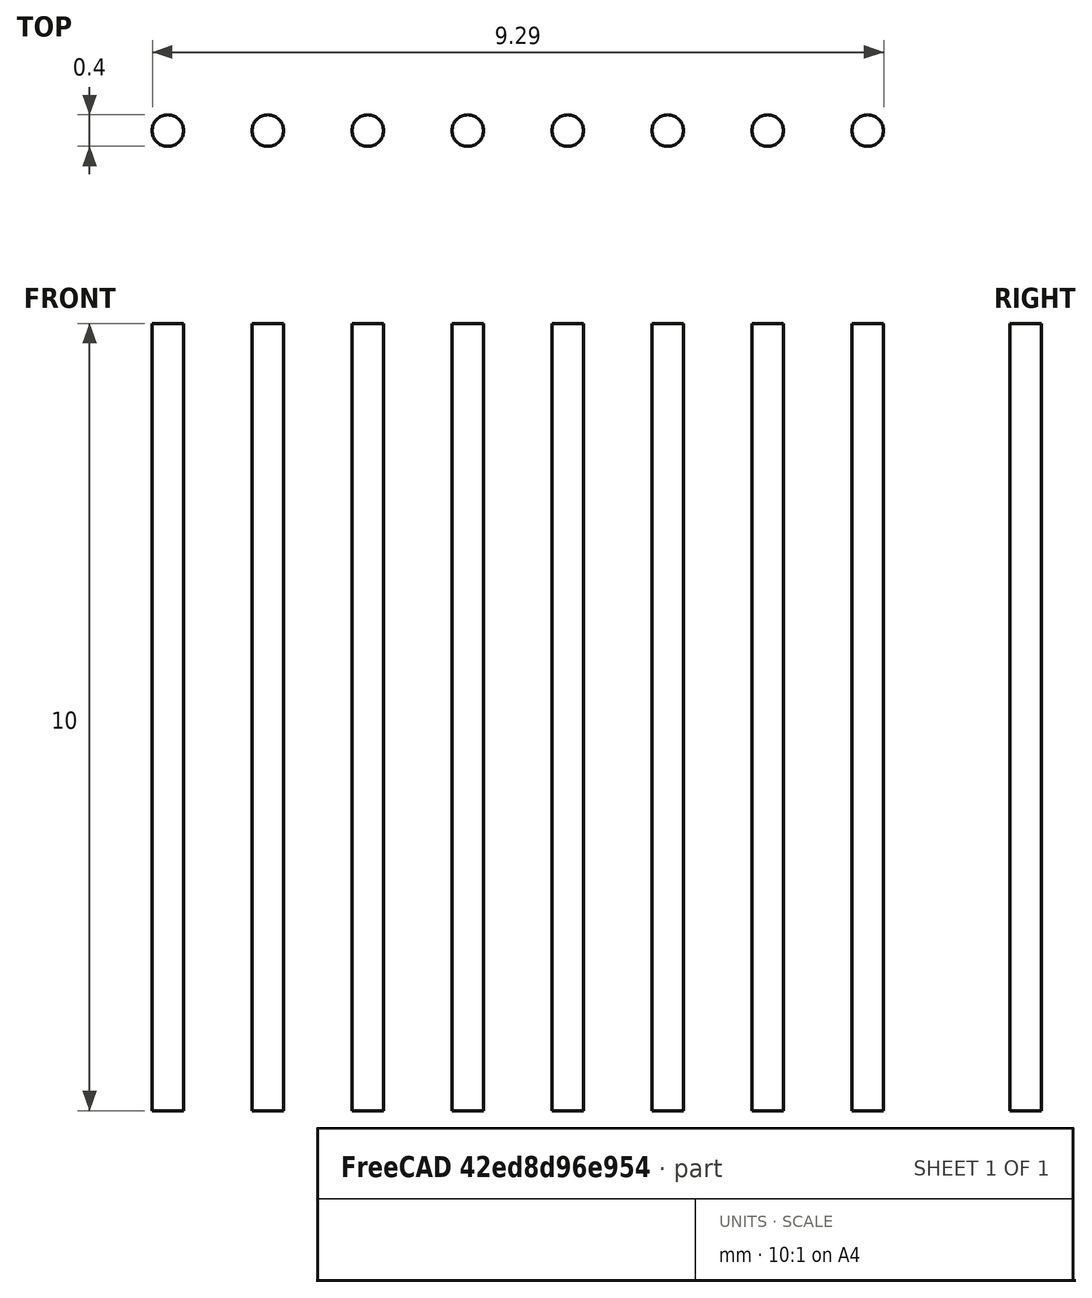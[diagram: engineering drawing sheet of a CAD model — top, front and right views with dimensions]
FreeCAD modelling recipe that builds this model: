
FCSTD DOCUMENT  (FreeCAD 0.14R3702 (Git))
Label: LCD
License: CC-BY 3.0
LicenseURL: http://creativecommons.org/licenses/by/3.0/
objects: Sketcher::SketchObject×2, Part::Cylinder×1, Part::FeaturePython×1, Part::Part2DObjectPython×1
note: 5 computed .brp shape members not serialized (recipe doc carries the construction recipe); baked Part::Feature solids carry a one-line shape summary decoded from their .brp

FEATURE [Sketcher::SketchObject] Sketch
  sketch-geometry (16):
    g0: LineSegment StartX=0 StartY=20.7 StartZ=0 EndX=51.2 EndY=20.7 EndZ=0
    g1: LineSegment StartX=51.2 StartY=20.7 StartZ=0 EndX=51.2 EndY=0 EndZ=0
    g2: LineSegment StartX=51.2 StartY=0 StartZ=0 EndX=0 EndY=0 EndZ=0
    g3: LineSegment StartX=0 StartY=0 StartZ=0 EndX=0 EndY=20.7 EndZ=0
    g4: LineSegment StartX=50.35 StartY=16.35 StartZ=0 EndX=50.35 EndY=14.35 EndZ=0
    g5: LineSegment StartX=49.75 StartY=14.35 StartZ=0 EndX=49.75 EndY=16.35 EndZ=0
    g6: LineSegment StartX=50.35 StartY=6.35 StartZ=0 EndX=50.35 EndY=4.35 EndZ=0
    g7: LineSegment StartX=49.75 StartY=4.35 StartZ=0 EndX=49.75 EndY=6.35 EndZ=0
    g8: GeomPoint [constr] X=50.05 Y=6.35 Z=0
    g9: ArcOfCircle CenterX=50.05 CenterY=6.35 CenterZ=0 NormalX=0 NormalY=0 NormalZ=1 Radius=0.3 StartAngle=0 EndAngle=3.14159
    g10: GeomPoint [constr] X=50.05 Y=4.35 Z=0
    g11: ArcOfCircle CenterX=50.05 CenterY=4.35 CenterZ=0 NormalX=0 NormalY=0 NormalZ=1 Radius=0.3 StartAngle=3.14159 EndAngle=6.28319
    g12: GeomPoint [constr] X=50.05 Y=16.35 Z=0
    g13: GeomPoint [constr] X=50.05 Y=14.35 Z=0
    g14: ArcOfCircle CenterX=50.05 CenterY=16.35 CenterZ=0 NormalX=0 NormalY=0 NormalZ=1 Radius=0.3 StartAngle=0 EndAngle=3.14159
    g15: ArcOfCircle CenterX=50.05 CenterY=14.3509 CenterZ=0 NormalX=0 NormalY=0 NormalZ=1 Radius=0.300001 StartAngle=3.14456 EndAngle=6.28021
  constraints (30):
    c: Coincident(g0,g1)
    c: Coincident(g1,g2)
    c: Coincident(g2,g3)
    c: Coincident(g3,g0)
    c: Horizontal(g0)
    c: Horizontal(g2)
    c: Vertical(g1)
    c: Vertical(g3)
    c: DistanceX(g0) = 51.2
    c: DistanceY(g1) = -20.7
    c: Vertical(g4)
    c: Vertical(g5)
    c: DistanceY(g4) = -2
    c: Vertical(g6)
    c: Vertical(g7)
    c: DistanceY(g6) = -2
    c: DistanceX(g5,g7) = 0
    c: DistanceY(g4,g6) = -8
    c: DistanceX(g4,g0) = 0.85
    c: Coincident(g2,g-1)
    c: DistanceY(g4,g0) = 4.35
    c: DistanceX(g7,g8) = 0.3
    c: Coincident(g9,g8)
    c: DistanceX(g10,g7) = -0.3
    c: Coincident(g11,g10)
    c: Coincident(g11,g6)
    c: DistanceX(g13,g5) = -0.3
    c: DistanceX(g12,g5) = -0.3
    c: Coincident(g14,g12)
    c: Coincident(g15,g4)
FEATURE [Part::Cylinder] Cylinder  label="Cilindro"
  Angle = 360
  Height = 10
  Placement = pos=(18.155,1.1,0) rot=(0,0,1;0rad)
  Radius = 0.2
FEATURE [Part::FeaturePython] Array001  label="pin3D"  # Draft array (typed FeaturePython)
  Angle = 360
  ArrayType = 0
  Axis = (0,0,1)
  Base = -> Cylinder
  Center = (0,0,0)
  IntervalX = (1.27,0,0)
  IntervalY = (0,1,0)
  IntervalZ = (0,0,1)
  NumberPolar = 1
  NumberX = 8
  NumberY = 1
  NumberZ = 1
FEATURE [Part::Part2DObjectPython] Shape2DView  label="pin3Da2D"  # Draft 2D object (typed FeaturePython)
  Base = -> Array001
  HiddenLines = false
  Projection = (0,0,1)
  ProjectionMode = 0
  SegmentLength = 0.05
  Tessellation = false
FEATURE [Sketcher::SketchObject] Sketch001  label="pin3Da2DSketch"
  sketch-geometry (8):
    g0: Circle CenterX=18.155 CenterY=1.1 CenterZ=0 NormalX=0 NormalY=0 NormalZ=1 Radius=0.2
    g1: Circle CenterX=19.425 CenterY=1.1 CenterZ=0 NormalX=0 NormalY=0 NormalZ=1 Radius=0.2
    g2: Circle CenterX=20.695 CenterY=1.1 CenterZ=0 NormalX=0 NormalY=0 NormalZ=1 Radius=0.2
    g3: Circle CenterX=21.965 CenterY=1.1 CenterZ=0 NormalX=0 NormalY=0 NormalZ=1 Radius=0.2
    g4: Circle CenterX=23.235 CenterY=1.1 CenterZ=0 NormalX=0 NormalY=0 NormalZ=1 Radius=0.2
    g5: Circle CenterX=24.505 CenterY=1.1 CenterZ=0 NormalX=0 NormalY=0 NormalZ=1 Radius=0.2
    g6: Circle CenterX=25.775 CenterY=1.1 CenterZ=0 NormalX=0 NormalY=0 NormalZ=1 Radius=0.2
    g7: Circle CenterX=27.045 CenterY=1.1 CenterZ=0 NormalX=0 NormalY=0 NormalZ=1 Radius=0.2
